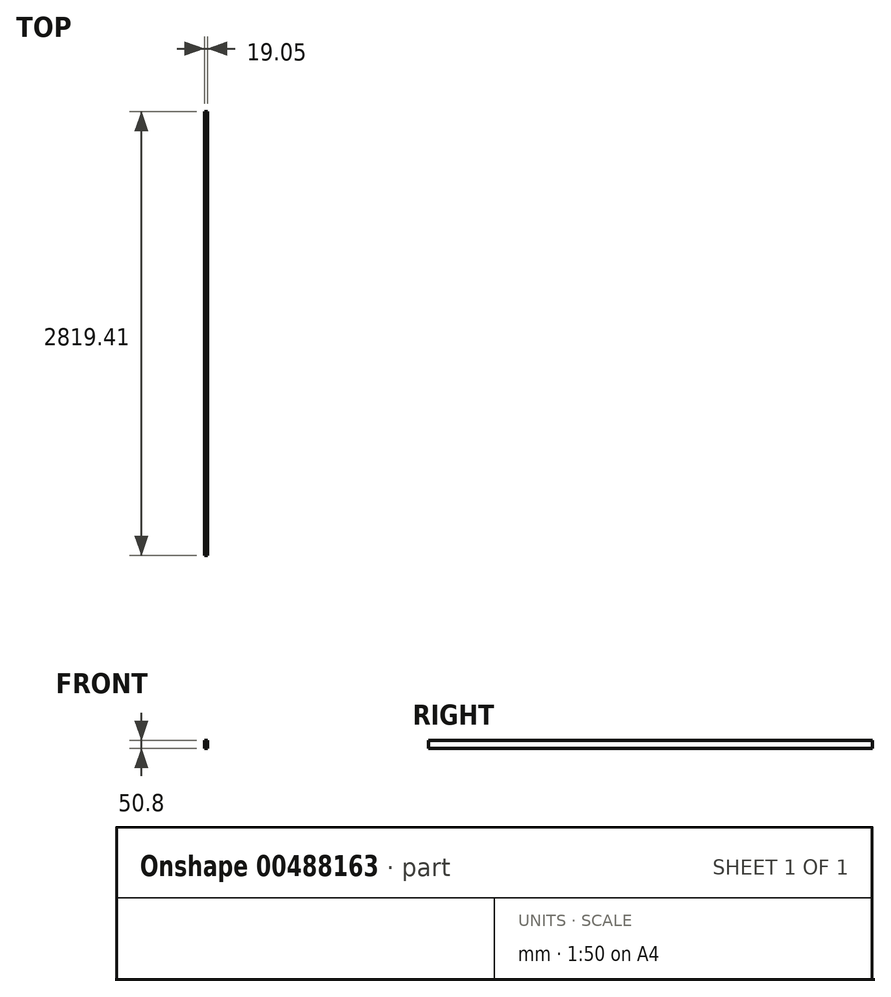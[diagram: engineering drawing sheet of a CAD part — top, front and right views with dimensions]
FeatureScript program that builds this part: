
annotation { "Feature Type Name" : "Feature", "Feature Type Description" : "" }
export const myFeature = defineFeature(function(context is Context, id is Id, definition is map)
    precondition{}
    {
        {
            var Q0;
            Q0=qCreatedBy(makeId("Front.planeOp"),FACE);
            var sketch = newSketch(context, id + "F0", { "sketchPlane" : qUnion([Q0])});
            skLineSegment(sketch, "E0", {"start": v(0, 0) * mm, "end": v(19.05, 0) * mm});
            skLineSegment(sketch, "E1", {"start": v(0, 0) * mm, "end": v(0, -50.8) * mm});
            skLineSegment(sketch, "E2", {"start": v(0, -50.8) * mm, "end": v(19.05, -50.8) * mm});
            skLineSegment(sketch, "E3", {"start": v(19.05, -50.8) * mm, "end": v(19.05, 0) * mm});
            skSolve(sketch);
        }
        {
            var Q0;
            Q0=makeQuery(id+"F0.imprint","IMPRINT",FACE,{"disambiguationData":[TD([[makeQuery(id+"F0.imprint","IMPRINT",EDGE,{"derivedFrom":sQuery(id+"F0.wireOp",EDGE,"E0")}),-1.0]])]});
            extrude(context, id + "F1", {"entities" : qUnion([Q0]), "oppositeDirection" : true, "depth" : 2743.2 * mm + 76.2 * mm + 1 / 76.2 * mm, "offsetDistance" : 25.4 * mm});
        }
    });
